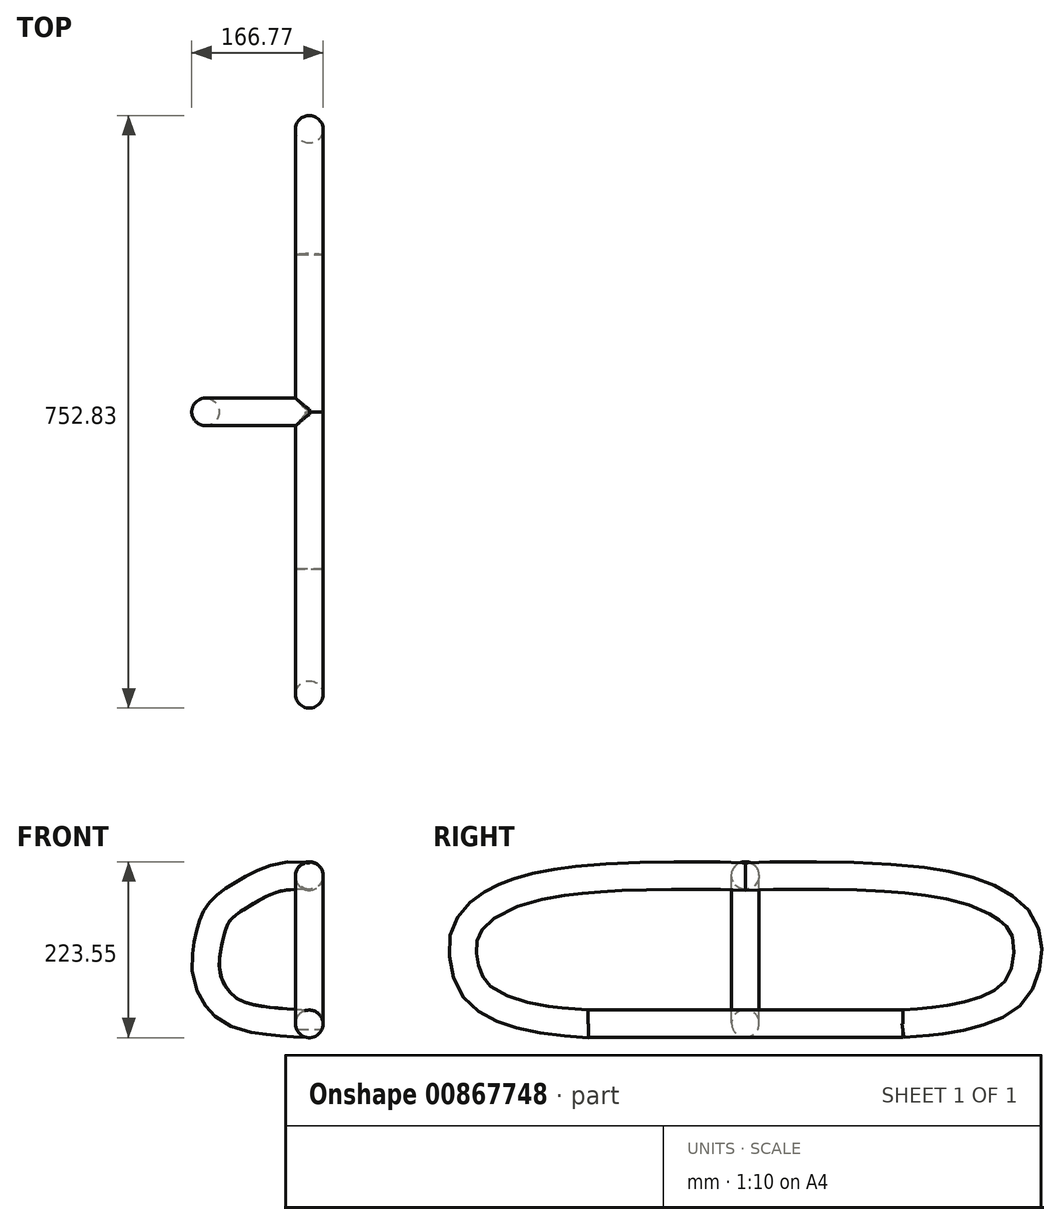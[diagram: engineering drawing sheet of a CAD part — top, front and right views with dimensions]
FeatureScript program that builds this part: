
annotation { "Feature Type Name" : "Feature", "Feature Type Description" : "" }
export const myFeature = defineFeature(function(context is Context, id is Id, definition is map)
    precondition{}
    {
        {
            var Q0;
            Q0=qCreatedBy(makeId("Front.planeOp"),FACE);
            var sketch = newSketch(context, id + "F0", { "sketchPlane" : qUnion([Q0])});
            skCircle(sketch, "E0", {"center": v(0, 0) * mm, "radius": 17.5 * mm});
            skSolve(sketch);
        }
        {
            var Q0;
            Q0=makeQuery(id+"F0.imprint","IMPRINT",FACE,{"disambiguationData":[TD([[makeQuery(id+"F0.imprint","IMPRINT",EDGE,{"derivedFrom":sQuery(id+"F0.wireOp",EDGE,"E0")}),1.0]])]});
            extrude(context, id + "F1", {"entities" : qUnion([Q0]), "depth" : 200 * mm, "offsetDistance" : 25 * mm, "hasSecondDirection" : true, "secondDirectionOppositeDirection" : true, "secondDirectionDepth" : 200 * mm});
        }
        {
            var Q0;
            Q0=qCreatedBy(makeId("Right.planeOp"),FACE);
            var sketch = newSketch(context, id + "F2", { "sketchPlane" : qUnion([Q0])});
            skPoint(sketch, "E1.0.internal.orphan", {"position": v(-201.09, 0) * mm});
            skPoint(sketch, "E1.7.internal.orphan", {"position": v(0, 238.65) * mm});
            skPoint(sketch, "E2.0.internal.orphan", {"position": v(-198.98, 0) * mm});
            skLineSegment(sketch, "E3", {"start": v(0, 0) * mm, "end": v(0, 187) * mm});
            skFitSpline(sketch, "E4", {"points": [v(-198.98, 0) * mm, v(-277.82, 9.81) * mm, v(-339.69, 38.98) * mm, v(-358.25, 84.06) * mm, v(-350.3, 127.37) * mm, v(-295.5, 165.38) * mm, v(-198.98, 183.94) * mm, v(-83.36, 188.36) * mm, v(0, 187) * mm], "startDerivative": vector(-611.75, 44.9) * mm, "endDerivative": vector(597.57, -20.22) * mm});
            skFitSpline(sketch, "E5.MirrorCS", {"points": [v(198.98, 0) * mm, v(277.82, 9.81) * mm, v(339.69, 38.98) * mm, v(358.25, 84.06) * mm, v(350.3, 127.37) * mm, v(295.5, 165.38) * mm, v(198.98, 183.94) * mm, v(83.36, 188.36) * mm, v(0, 187) * mm], "startDerivative": vector(611.75, 44.9) * mm, "endDerivative": vector(-597.57, -20.22) * mm});
            skSolve(sketch);
        }
        {
            var Q0;
            Q0=makeQuery(id+"F1.opExtrude","CAP_FACE",FACE,{"disambiguationData":[OSD([sQuery(id+"F0.wireOp",EDGE,"E0")])],"isStart":false});
            var Q1;
            Q1=sQuery(id+"F2.wireOp",EDGE,"E4");
            var Q2;
            Q2=sQuery(id+"F2.wireOp",EDGE,"E5.MirrorCS");
            sweep(context, id + "F3", {"operationType" : NewBodyOperationType.ADD, "profiles" : qUnion([Q0]), "path" : qUnion([Q1, Q2])});
        }
        {
            var Q0;
            Q0=qCreatedBy(makeId("Front.planeOp"),FACE);
            var sketch = newSketch(context, id + "F4", { "sketchPlane" : qUnion([Q0])});
            skFitSpline(sketch, "E6", {"points": [v(0, 0) * mm, v(-77.75, 8) * mm, v(-111.52, 25.77) * mm, v(-131.07, 64.87) * mm, v(-125.74, 114.63) * mm, v(-115.08, 141.3) * mm, v(-91.08, 160.84) * mm, v(-41.32, 185.72) * mm, v(0, 187.5) * mm], "startDerivative": vector(-519.14, 26.86) * mm, "endDerivative": vector(333.34, -26.8) * mm});
            skSolve(sketch);
        }
        {
            var Q0;
            Q0=qCreatedBy(makeId("Right.planeOp"),FACE);
            var sketch = newSketch(context, id + "F5", { "sketchPlane" : qUnion([Q0])});
            skCircle(sketch, "E7", {"center": v(0, 0) * mm, "radius": 17.5 * mm});
            skSolve(sketch);
        }
        {
            var Q0;
            Q0 = qSketchRegion(id + "F5", true);
            var Q1;
            Q1=sQuery(id+"F4.wireOp",EDGE,"E6");
            sweep(context, id + "F6", {"operationType" : NewBodyOperationType.ADD, "profiles" : qUnion([Q0]), "path" : qUnion([Q1])});
        }
    });
